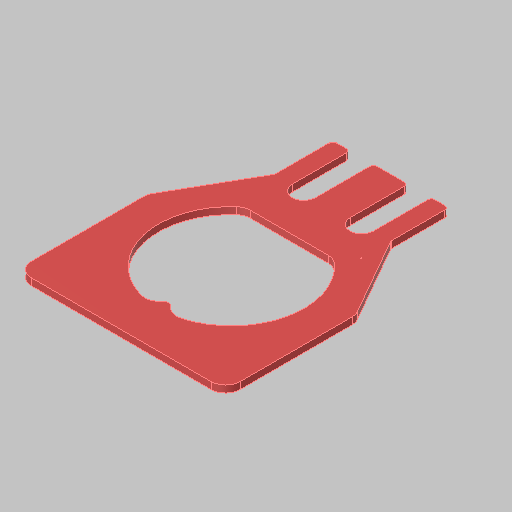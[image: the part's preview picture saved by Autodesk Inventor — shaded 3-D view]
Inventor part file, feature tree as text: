
AUTODESK INVENTOR PART (.ipt)
format: ipt  version: 2023.5 (Build 275446000, 446)  size: 291,840 bytes
history: native  units: in
note: dims shown in document units (in); Inventor stores cm internally (conversion verified against a paired STEP export)
features: sketch x6, extrude x6, fillet x5, projected_geometry x5
ambient origin geometry x8: Origin, YZ Plane, XZ Plane, XY Plane, X Axis, Y Axis, Z Axis, Center Point
bodies: Solid1 (feature_tree)
feature tree (22):
  sketch  "Sketch1"  dims[d1=0.7in d3=0.125in d4=0.197in]
  extrude  "Extrusion1"  Depth=0.125in
  fillet  "Fillet1"  Radius=0.197in
  extrude  "Extrusion2"  Depth=1.0in
  extrude  "Extrusion3"  Depth=0.5in
  fillet  "Fillet2"  Radius=0.5in
  extrude  "Extrusion4"  Depth=0.06in TaperAngle=0.0deg
  fillet  "Fillet3"  Radius=0.125in
  extrude  "Extrusion5"  Depth=0.5in
  fillet  "Fillet4"  Radius=1.375in
  extrude  "Extrusion6"  Depth=1.0in TaperAngle=0.0deg
  fillet  "Fillet5"  Radius=1.26in
  sketch  "Sketch2"  dims[d5=0.197in d8=1.0in]
  sketch  "Sketch3"  dims[d9=2.0in d10=0.25in d11=0.5in]
  sketch  "Sketch4"  dims[d12=0.25in d13=0.06in d14=0.0in d22=0.125in]
  sketch  "Sketch5"  dims[d23=0.201in d24=0.5in d26=1.375in]
  sketch  "Sketch6"  dims[d27=0.5in d28=1.0in d29=0.0in d30=1.26in d31=0.5in d32=0.125in d33=1.0in d34=0.0in d35=0.125in d36=0.093in d37=0.042in d38=1.0in d39=0.0in d40=0.125in d41=0.7874in d43=0.197in d44=0.3937in d46=1.0in d48=1.8in d49=3.45in d50=1.125in d51=1.0in d52=0.0in d53=0.125in d54=1.25in d55=1.0in d57=0.0in d58=0.0in d59=0.0312in]
  projected_geometry  "Project Cut Edges1"
  projected_geometry  "Project Cut Edges2"
  projected_geometry  "Project Cut Edges3"
  projected_geometry  "Project Cut Edges4"
  projected_geometry  "Project Cut Edges5"
